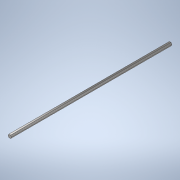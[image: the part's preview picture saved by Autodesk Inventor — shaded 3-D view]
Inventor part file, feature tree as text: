
AUTODESK INVENTOR PART (.ipt)
format: ipt  version: 2020 (Build 240168000, 168)  size: 108,032 bytes
history: native  units: in
note: dims shown in document units (in); Inventor stores cm internally (conversion verified against a paired STEP export)
features: extrude x1, sketch x1
ambient origin geometry x8: Origin, YZ Plane, XZ Plane, XY Plane, X Axis, Y Axis, Z Axis, Center Point
bodies: Solid1 (feature_tree)
feature tree (2):
  extrude  "Extrusion1"  Depth=27.0in TaperAngle=0.0deg
  sketch  "Sketch1"  dims[d0=0.5in d1=27.0in d2=0.0in]
